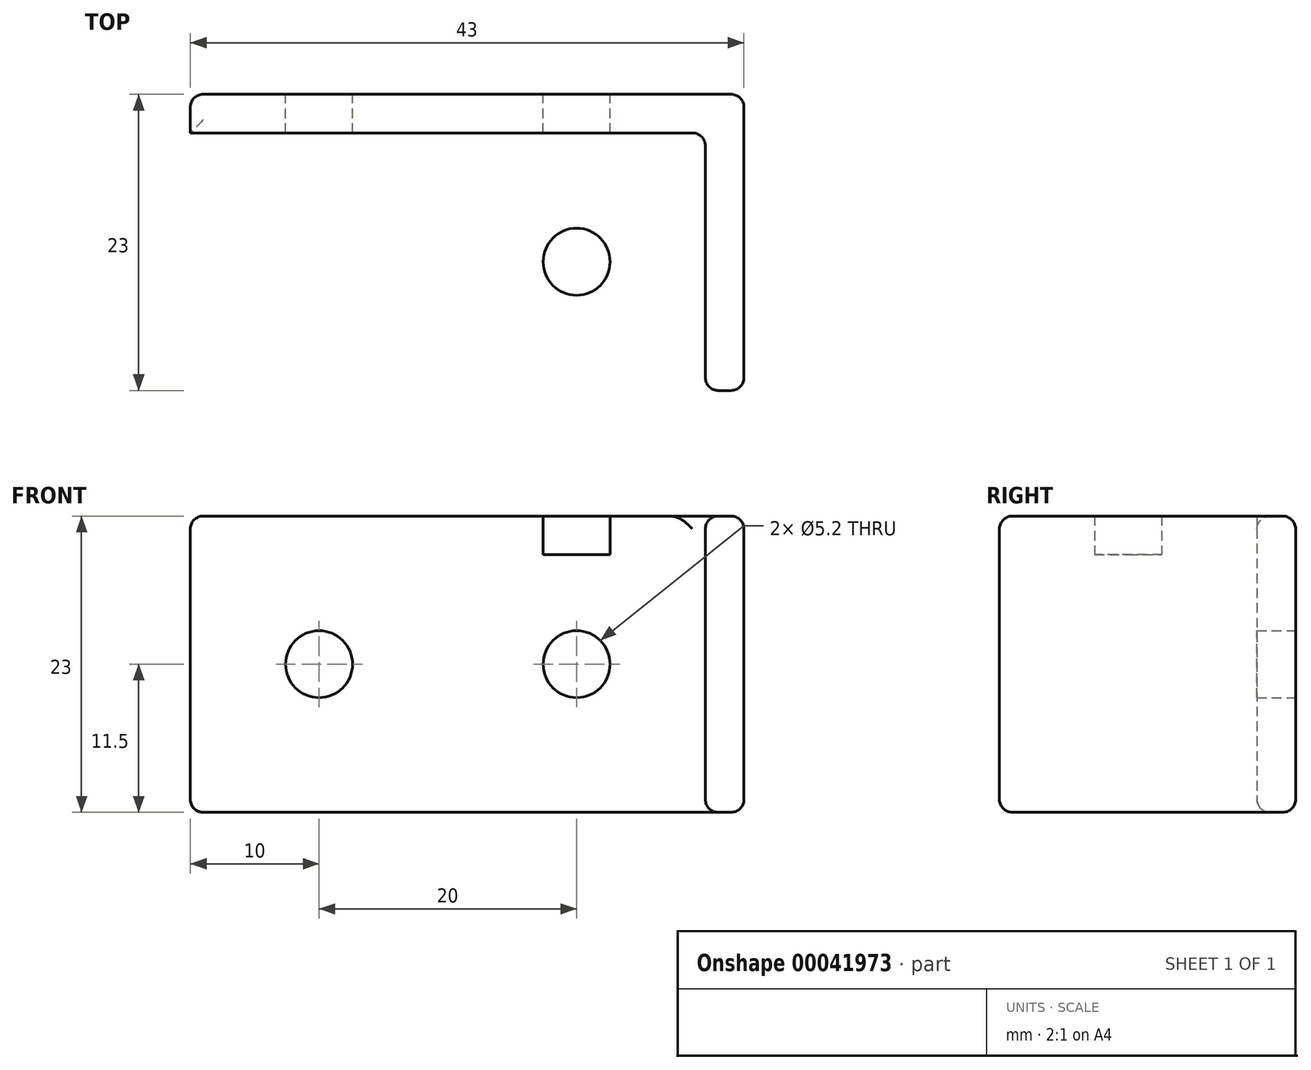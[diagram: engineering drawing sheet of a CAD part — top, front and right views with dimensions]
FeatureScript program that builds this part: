
annotation { "Feature Type Name" : "Feature", "Feature Type Description" : "" }
export const myFeature = defineFeature(function(context is Context, id is Id, definition is map)
    precondition{}
    {
        {
            var Q0;
            Q0=qCreatedBy(makeId("Front.planeOp"),FACE);
            var sketch = newSketch(context, id + "F0", { "sketchPlane" : qUnion([Q0])});
            skLineSegment(sketch, "E0.rect.bottom", {"start": v(21.5, 11.5) * mm, "end": v(-21.5, 11.5) * mm});
            skLineSegment(sketch, "E0.rect.top", {"start": v(21.5, -11.5) * mm, "end": v(-21.5, -11.5) * mm});
            skLineSegment(sketch, "E0.rect.left", {"start": v(21.5, 11.5) * mm, "end": v(21.5, -11.5) * mm});
            skLineSegment(sketch, "E0.rect.right", {"start": v(-21.5, 11.5) * mm, "end": v(-21.5, -11.5) * mm});
            skPoint(sketch, "E0.rect.middle", {"position": v(0, 0) * mm});
            skCircle(sketch, "E1", {"center": v(-11.5, 0) * mm, "radius": 2.6 * mm});
            skCircle(sketch, "E2", {"center": v(8.5, 0) * mm, "radius": 2.6 * mm});
            skSolve(sketch);
        }
        {
            var Q0;
            {var subQ2=sQuery(id+"F0.wireOp",EDGE,"E0.rect.left");Q0=makeQuery(id+"F0.imprint","IMPRINT",FACE,{"disambiguationData":[TD([[makeQuery(id+"F0.imprint","IMPRINT",EDGE,{"derivedFrom":subQ2}),-1.0]])]});}
            extrude(context, id + "F1", {"entities" : qUnion([Q0]), "endBound" : BoundingType.SYMMETRIC, "depth" : 3 * mm});
        }
        {
            var Q0;
            Q0=makeQuery(id+"F1.opExtrude","CAP_FACE",FACE,{"disambiguationData":[OSD([sQuery(id+"F0.wireOp",EDGE,"E0.rect.bottom"),sQuery(id+"F0.wireOp",EDGE,"E0.rect.top"),sQuery(id+"F0.wireOp",EDGE,"E0.rect.left"),sQuery(id+"F0.wireOp",EDGE,"E0.rect.right"),sQuery(id+"F0.wireOp",EDGE,"E1"),sQuery(id+"F0.wireOp",EDGE,"E2")])],"isStart":false});
            var sketch = newSketch(context, id + "F2", { "sketchPlane" : qUnion([Q0])});
            skLineSegment(sketch, "E3.0", {"start": v(21.5, 11.5) * mm, "end": v(-21.5, 11.5) * mm});
            skLineSegment(sketch, "E4.0", {"start": v(21.5, 11.5) * mm, "end": v(21.5, -11.5) * mm});
            skLineSegment(sketch, "E5.0", {"start": v(18.5, 8.5) * mm, "end": v(-21.5, 8.5) * mm});
            skLineSegment(sketch, "E5.1", {"start": v(18.5, 8.5) * mm, "end": v(18.5, -11.5) * mm});
            skLineSegment(sketch, "E6.0", {"start": v(-21.5, 11.5) * mm, "end": v(-21.5, -11.5) * mm});
            skSolve(sketch);
        }
        {
            var Q0;
            {var subQ2=sQuery(id+"F2.wireOp",EDGE,"E3.0");Q0=makeQuery(id+"F2.imprint","IMPRINT",FACE,{"disambiguationData":[TD([[makeQuery(id+"F2.imprint","IMPRINT",EDGE,{"derivedFrom":subQ2}),1.0]])]});}
            extrude(context, id + "F3", {"entities" : qUnion([Q0]), "operationType" : NewBodyOperationType.ADD, "depth" : 20 * mm});
        }
        {
            var Q0;
            Q0=makeQuery(id+"F3.opExtrude","SWEPT_FACE",FACE,{"disambiguationData":[OSD([sQuery(id+"F2.wireOp",EDGE,"E5.0")])]});
            var sketch = newSketch(context, id + "F4", { "sketchPlane" : qUnion([Q0])});
            skLineSegment(sketch, "E7", {"start": v(5.9, -1.5) * mm, "end": v(5.9, 1.5) * mm});
            skLineSegment(sketch, "E8", {"start": v(11.1, 1.5) * mm, "end": v(11.1, -1.5) * mm});
            skLineSegment(sketch, "E9", {"start": v(5.9, 1.5) * mm, "end": v(11.1, 21.5) * mm});
            skCircle(sketch, "E10", {"center": v(8.5, 11.5) * mm, "radius": 2.6 * mm});
            skSolve(sketch);
        }
        {
            var Q0;
            {var subQ0=sQuery(id+"F4.wireOp",EDGE,"E10");var subQ1=sQuery(id+"F4.wireOp",EDGE,"E9");var subQ3=makeQuery(id+"F4.imprint","INTERSECT",VERTEX,{"disambiguationData":[OD(0.0)],"derivedFrom":[subQ1,subQ0]});Q0=makeQuery(id+"F4.imprint","IMPRINT",FACE,{"disambiguationData":[TD([[makeQuery(id+"F4.imprint","IMPRINT",EDGE,{"disambiguationData":[TD([[subQ3,-1.0]])],"derivedFrom":subQ1}),1.0]])]});}
            var Q1;
            {var subQ0=sQuery(id+"F4.wireOp",EDGE,"E10");var subQ1=sQuery(id+"F4.wireOp",EDGE,"E9");var subQ3=makeQuery(id+"F4.imprint","INTERSECT",VERTEX,{"disambiguationData":[OD(0.0)],"derivedFrom":[subQ1,subQ0]});Q1=makeQuery(id+"F4.imprint","IMPRINT",FACE,{"disambiguationData":[TD([[makeQuery(id+"F4.imprint","IMPRINT",EDGE,{"disambiguationData":[TD([[subQ3,-1.0]])],"derivedFrom":subQ1}),-1.0]])]});}
            extrude(context, id + "F5", {"entities" : qUnion([Q0, Q1]), "operationType" : NewBodyOperationType.REMOVE, "endBound" : BoundingType.THROUGH_ALL, "oppositeDirection" : true, "depth" : 25.4 * mm});
        }
        {
            var Q0;
            Q0=makeQuery(id+"F3.opExtrude","SWEPT_FACE",FACE,{"disambiguationData":[OSD([sQuery(id+"F2.wireOp",EDGE,"E5.0")])]});
            var sketch = newSketch(context, id + "F6", { "sketchPlane" : qUnion([Q0])});
            skLineSegment(sketch, "E11.0", {"start": v(18.5, 21.5) * mm, "end": v(-21.5, 21.5) * mm});
            skLineSegment(sketch, "E12.0", {"start": v(-21.5, 21.5) * mm, "end": v(-21.5, 1.5) * mm});
            skLineSegment(sketch, "E13", {"start": v(-21.5, 3.5) * mm, "end": v(3.5, 21.5) * mm});
            skSolve(sketch);
        }
        {
            var Q0;
            {var subQ0=sQuery(id+"F6.wireOp",EDGE,"E13");Q0=makeQuery(id+"F6.imprint","IMPRINT",FACE,{"disambiguationData":[TD([[makeQuery(id+"F6.imprint","IMPRINT",EDGE,{"derivedFrom":subQ0}),1.0]])]});}
            extrude(context, id + "F7", {"entities" : qUnion([Q0]), "operationType" : NewBodyOperationType.REMOVE, "endBound" : BoundingType.THROUGH_ALL, "oppositeDirection" : true, "depth" : 25.4 * mm});
        }
        {
            var Q0;
            Q0=makeQuery(id+"F3.boolean.opBoolean","MERGE",FACE,{"derivedFrom":[makeQuery(id+"F1.opExtrude","SWEPT_FACE",FACE,{"disambiguationData":[OSD([sQuery(id+"F0.wireOp",EDGE,"E0.rect.left")])]}),makeQuery(id+"F3.opExtrude","SWEPT_FACE",FACE,{"disambiguationData":[OSD([sQuery(id+"F2.wireOp",EDGE,"E4.0")])]})]});
            var Q1;
            Q1=makeQuery(id+"F1.opExtrude","CAP_EDGE",EDGE,{"disambiguationData":[OSD([sQuery(id+"F0.wireOp",EDGE,"E0.rect.top")])],"isStart":true});
            var Q2;
            Q2=makeQuery(id+"F1.opExtrude","CAP_EDGE",EDGE,{"disambiguationData":[OSD([sQuery(id+"F0.wireOp",EDGE,"E0.rect.bottom")])],"isStart":true});
            var Q3;
            Q3=makeQuery(id+"F3.boolean.opBoolean","MERGE",EDGE,{"derivedFrom":[makeQuery(id+"F1.opExtrude","SWEPT_EDGE",EDGE,{"disambiguationData":[OSD([sQuery(id+"F0.wireOp",EDGE,"E0.rect.bottom"),sQuery(id+"F0.wireOp",EDGE,"E0.rect.right")])]}),makeQuery(id+"F3.opExtrude","SWEPT_EDGE",EDGE,{"disambiguationData":[OSD([sQuery(id+"F2.wireOp",EDGE,"E3.0"),sQuery(id+"F2.wireOp",EDGE,"E6.0")])]})]});
            var Q4;
            Q4=makeQuery(id+"F7.boolean.opBoolean","INTERSECT",EDGE,{"derivedFrom":[makeQuery(id+"F3.boolean.opBoolean","MERGE",FACE,{"derivedFrom":[makeQuery(id+"F1.opExtrude","SWEPT_FACE",FACE,{"disambiguationData":[OSD([sQuery(id+"F0.wireOp",EDGE,"E0.rect.bottom")])]}),makeQuery(id+"F3.opExtrude","SWEPT_FACE",FACE,{"disambiguationData":[OSD([sQuery(id+"F2.wireOp",EDGE,"E3.0")])]})]}),makeQuery(id+"F7.opExtrude","SWEPT_FACE",FACE,{"disambiguationData":[OSD([sQuery(id+"F6.wireOp",EDGE,"E13")])]})]});
            var Q5;
            Q5=makeQuery(id+"F3.opExtrude","CAP_EDGE",EDGE,{"disambiguationData":[OSD([sQuery(id+"F2.wireOp",EDGE,"E3.0")])],"isStart":false});
            var Q6;
            Q6=makeQuery(id+"F7.boolean.opBoolean","COPY",EDGE,{"derivedFrom":makeQuery(id+"F7.opExtrude","CAP_EDGE",EDGE,{"disambiguationData":[OSD([sQuery(id+"F6.wireOp",EDGE,"E13")])],"isStart":true})});
            var Q7;
            Q7=makeQuery(id+"F7.boolean.opBoolean","COPY",EDGE,{"derivedFrom":makeQuery(id+"F7.opExtrude","SWEPT_EDGE",EDGE,{"disambiguationData":[OSD([sQuery(id+"F6.wireOp",EDGE,"E11.0"),sQuery(id+"F6.wireOp",EDGE,"E13")])]})});
            var Q8;
            Q8=makeQuery(id+"F3.opExtrude","CAP_EDGE",EDGE,{"disambiguationData":[OSD([sQuery(id+"F2.wireOp",EDGE,"E5.0")])],"isStart":false});
            var Q9;
            Q9=makeQuery(id+"F3.opExtrude","CAP_EDGE",EDGE,{"disambiguationData":[OSD([sQuery(id+"F2.wireOp",EDGE,"E5.1")])],"isStart":false});
            var Q10;
            Q10=makeQuery(id+"F1.opExtrude","CAP_EDGE",EDGE,{"disambiguationData":[OSD([sQuery(id+"F0.wireOp",EDGE,"E0.rect.top")])],"isStart":false});
            var Q11;
            Q11=makeQuery(id+"F3.opExtrude","SWEPT_FACE",FACE,{"disambiguationData":[OSD([sQuery(id+"F2.wireOp",EDGE,"E5.1")])]});
            var Q12;
            {var subQ0=sQuery(id+"F0.wireOp",EDGE,"E0.rect.top");Q12=makeQuery(id+"F3.boolean.opBoolean","MERGE",FACE,{"derivedFrom":[makeQuery(id+"F1.opExtrude","SWEPT_FACE",FACE,{"disambiguationData":[OSD([subQ0])]}),makeQuery(id+"F3.opExtrude","SWEPT_FACE",FACE,{"disambiguationData":[OSD([subQ0])]})]});}
            var Q13;
            Q13=makeQuery(id+"F1.opExtrude","CAP_EDGE",EDGE,{"disambiguationData":[OSD([sQuery(id+"F0.wireOp",EDGE,"E0.rect.right")])],"isStart":true});
            var Q14;
            Q14=makeQuery(id+"F1.opExtrude","CAP_EDGE",EDGE,{"disambiguationData":[OSD([sQuery(id+"F0.wireOp",EDGE,"E0.rect.right")])],"isStart":false});
            var Q15;
            Q15=makeQuery(id+"F3.opExtrude","SWEPT_EDGE",EDGE,{"disambiguationData":[OSD([sQuery(id+"F2.wireOp",EDGE,"E5.0"),sQuery(id+"F2.wireOp",EDGE,"E6.0")])]});
            var Q16;
            Q16=makeQuery(id+"F7.boolean.opBoolean","COPY",EDGE,{"derivedFrom":makeQuery(id+"F7.opExtrude","SWEPT_EDGE",EDGE,{"disambiguationData":[OSD([sQuery(id+"F6.wireOp",EDGE,"E12.0"),sQuery(id+"F6.wireOp",EDGE,"E13")])]})});
            var Q17;
            Q17=makeQuery(id+"F3.opExtrude","CAP_EDGE",EDGE,{"disambiguationData":[OSD([sQuery(id+"F2.wireOp",EDGE,"E5.0")])],"isStart":true});
            fillet(context, id + "F8", {"entities" : qUnion([Q0, Q1, Q2, Q3, Q4, Q5, Q6, Q7, Q8, Q9, Q10, Q11, Q12, Q13, Q14, Q15, Q16, Q17]), "radius" : 1 * mm, "allowEdgeOverflow" : false});
        }
    });
